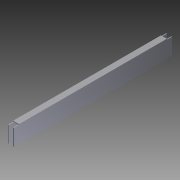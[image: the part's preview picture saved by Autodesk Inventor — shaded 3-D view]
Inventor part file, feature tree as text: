
AUTODESK INVENTOR PART (.ipt)
format: ipt  version: 2012 (Build 160160000, 160)  size: 106,496 bytes
history: native  units: in
note: dims shown in document units (in); Inventor stores cm internally (conversion verified against a paired STEP export)
features: extrude x3, sketch x3
ambient origin geometry x8: Origin, YZ Plane, XZ Plane, XY Plane, X Axis, Y Axis, Z Axis, Center Point
bodies: Solid1 (feature_tree)
feature tree (6):
  extrude  "Extrusion1"  Depth=3.0in
  extrude  "Extrusion2"  Depth=0.125in
  extrude  "Extrusion3"  Depth=0.125in
  sketch  "Sketch1"  dims[d0=1.0in d1=3.0in]
  sketch  "Sketch2"  dims[d2=0.125in d3=0.125in]
  sketch  "Sketch3"  dims[d4=0.125in d5=0.125in d6=26.75in d7=0.0in d8=0.875in d9=0.875in d10=0.125in d11=0.0in d12=0.875in d13=0.875in d14=0.125in d15=0.0in]
